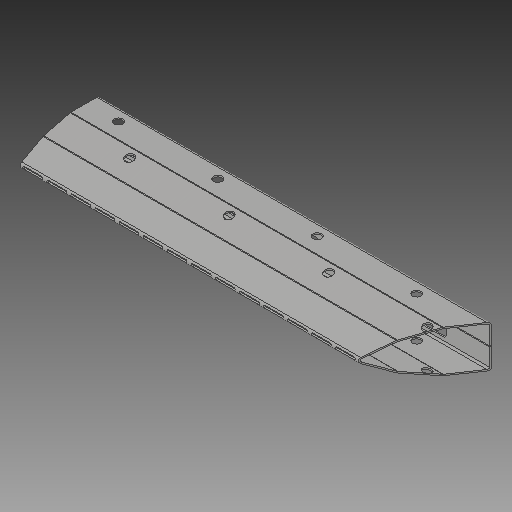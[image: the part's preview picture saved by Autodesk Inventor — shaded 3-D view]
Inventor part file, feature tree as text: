
AUTODESK INVENTOR PART (.ipt)
format: ipt  version: 2018 (Build 220112000, 112)  size: 884,224 bytes
history: native  units: mm
features: other x24, reference x24, sketch x16, sheet_metal_op x13, plane x9, projected_geometry x8, extrude x6
ambient origin geometry x8: Origin, YZ Plane, XZ Plane, XY Plane, X Axis, Y Axis, Z Axis, Center Point
bodies: Solid1 (feature_tree)
feature tree (100):
  parser-record x5  (decoder bookkeeping rows leaked as tree rows — omitted from the tree; the rows remain in map.json)
  plane  "Work Plane1"
  sheet_metal_op  "Face1"
  plane  "Work Plane2"
  sheet_metal_op  "Face2"
  plane  "Work Plane3"
  sheet_metal_op  "Face3"
  plane  "Work Plane4"
  sheet_metal_op  "Face4"
  plane  "Work Plane5"
  sheet_metal_op  "Face5"
  plane  "Work Plane6"
  sheet_metal_op  "Face6"
  plane  "Work Plane7"
  sheet_metal_op  "Face7"
  other  "midtplan"
  extrude  "afskær bund"  Depth=5.0mm
  extrude  "afskær top"  Depth=2.0mm
  extrude  "hulsæt til stifter"  Depth=5.0mm
  sketch  "Sketch14"  dims[d16=5.0mm]
  plane  "Work Plane12"
  extrude  "balusterhul"  Depth=4.0mm
  extrude  "balusterhul skråkompensering"  Depth=8.0mm
  extrude  "test"  Depth=5.0mm
  sketch  "Sketch1"  dims[d0=4.0mm d1=5.0mm]
  reference  "Reference1"
  reference  "Reference2"
  reference  "Reference3"
  reference  "Reference4"
  other  "Plate1"
  sketch  "Sketch2"  dims[d2=4.0mm d3=2.0mm]
  reference  "Reference5"
  reference  "Reference6"
  reference  "Reference7"
  reference  "Reference8"
  other  "Plate2"
  sheet_metal_op  "Bend1"
  sketch  "Sketch3"  dims[d4=8.0mm d5=5.0mm]
  reference  "Reference9"
  reference  "Reference10"
  reference  "Reference11"
  other  "Plate3"
  sheet_metal_op  "Bend2"
  sketch  "Sketch4"  dims[d6=5.0mm d7=4.0mm]
  reference  "Reference12"
  reference  "Reference13"
  reference  "Reference14"
  reference  "Reference15"
  other  "Plate4"
  sheet_metal_op  "Bend3"
  sketch  "Sketch5"  dims[d8=2.0mm d9=8.0mm]
  reference  "Reference16"
  reference  "Reference17"
  reference  "Reference18"
  other  "Plate5"
  sheet_metal_op  "Bend4"
  sketch  "Sketch6"  dims[d10=5.0mm d11=5.0mm]
  reference  "Reference19"
  reference  "Reference20"
  reference  "Reference21"
  other  "Plate6"
  sheet_metal_op  "Bend5"
  sketch  "Sketch7"  dims[d12=4.0mm]
  reference  "Reference22"
  reference  "Reference23"
  other  "Plate7"
  sheet_metal_op  "Bend6"
  sketch  "Sketch8"  dims[d13=2.0mm]
  reference  "Reference24"
  projected_geometry  "Projected Loop1"
  other  "huller til stifter"
  projected_geometry  "Projected Loop3"
  sketch  "Sketch12"  dims[d14=8.0mm]
  projected_geometry  "Projected Loop4"
  sketch  "Sketch13"  dims[d15=5.0mm]
  projected_geometry  "Projected Loop5"
  plane  "Work Plane11"
  sketch  "Sketch15"  dims[d17=4.0mm]
  sketch  "Sketch16"  dims[d18=2.0mm]
  projected_geometry  "Projected Loop6"
  projected_geometry  "Projected Loop7"
  sketch  "Sketch17"  dims[d19=8.0mm]
  projected_geometry  "Projected Loop8"
  projected_geometry  "Projected Loop9"
  sketch  "Sketch18"  dims[d20=5.0mm]
  sketch  "Sketch20"  dims[d21=5.0mm d22=4.0mm d23=2.0mm d24=8.0mm d25=5.0mm d26=5.0mm d27=4.0mm d28=2.0mm d29=8.0mm d30=5.0mm d31=4.0mm d32=0.0mm d33=3.0mm d39=250.0mm d41=33.7mm d42=33.7mm d43=60.0mm d44=70.0mm d45=16.85mm d46=65.0mm d47=60.0mm d48=10.0mm d49=0.0mm d50=250.0mm d51=33.7mm d52=33.7mm d53=60.0mm d54=16.85mm d55=65.0mm d56=60.0mm d57=30.0mm d59=302.736671mm d60=10.0mm d62=10.0mm d65=302.736671mm d66=195.343893mm d68=306.228mm d69=10.0mm d70=0.0mm d71=96.671937mm d74=10.0mm d75=0.0mm d76=5.986479mm d77=26.6mm d78=25.8mm d79=26.6mm d80=26.6mm d81=26.6mm d82=26.6mm d83=26.6mm d84=26.6mm d85=40.001254mm d95=113.170852mm d96=56.585426mm d97=90.0deg d98=49.5mm d99=100.0mm d100=0.0mm d101=2.728615mm d102=1.364307mm d103=10.0mm d104=0.0mm d105=90.0mm d106=342.765mm d107=342.765mm d108=30.0mm d109=30.0mm d110=30.0mm d111=342.765mm d112=10.0mm d113=4.0mm d114=0.0mm d115=6.0mm d116=61.0mm d117=8.0mm d118=150.0mm d120=73.2mm d121=10.0mm d123=10.0mm d125=4.0mm d126=0.0mm d129=10.0mm d130=0.0mm]
  other  "Cut1"
  other  "plantehuller"
  other  "bukkeperforering"
  other  "modul top.iam"
  other  "model:1"
  other  "Definition1"
  other  "modul.iam"
  other  "søjle+vange.iam"
  other  "stilladssøjle:2"
  other  "rør:1"
note: 5 file-system paths scrubbed to <path> (originals preserved in map.json)
